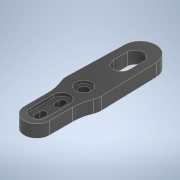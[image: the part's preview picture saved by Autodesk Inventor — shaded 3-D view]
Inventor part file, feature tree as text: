
AUTODESK INVENTOR PART (.ipt)
format: ipt  version: 2022.6 (Build 266554000, 554)  size: 199,680 bytes
history: native  units: mm
features: extrude x6, sketch x6, projected_geometry x1
ambient origin geometry x8: Origin, YZ Plane, XZ Plane, XY Plane, X Axis, Y Axis, Z Axis, Center Point
bodies: Solid1 (feature_tree)
feature tree (13):
  extrude  "Extrusion1"  Depth=3.0mm
  extrude  "Extrusion2"  Depth=4.0mm TaperAngle=0.0deg
  extrude  "Extrusion8"  Depth=5.2mm
  extrude  "Extrusion9"  TaperAngle=0.0deg  [1 undecoded]
  extrude  "Extrusion10"  Depth=4.0mm
  extrude  "Extrusion11"  Depth=1.0mm
  sketch  "Sketch1"  dims[d0=3.0mm d1=11.0mm]
  sketch  "Sketch2"  dims[d3=18.0mm d4=4.0mm d5=0.0mm]
  projected_geometry  "Projected Loop1"
  sketch  "Sketch8"  dims[d6=4.4mm d7=5.2mm]
  sketch  "Sketch10"  dims[d9=12.0mm d10=0.0mm d11=0.0mm]
  sketch  "Sketch11"  dims[d43=15.0mm d44=4.0mm]
  sketch  "Sketch12"  dims[d45=5.2mm d47=7.0mm d48=14.5mm d49=1.0mm d50=0.0mm d60=2.2mm d61=6.8mm d62=1.4mm d63=1.5mm d64=2.2mm d65=13.0mm d66=0.0mm d67=0.0mm d70=0.4mm d71=0.0mm d72=5.5mm d73=8.5mm d74=10.0mm d75=5.0mm d76=1.0mm d77=0.0mm d78=0.2mm d79=7.5mm]
note: 1 required parameter value undecoded (feature->parameter linkage not recoverable at this tier; creation-order binding heuristic only, values carry confidence <= 0.55)
